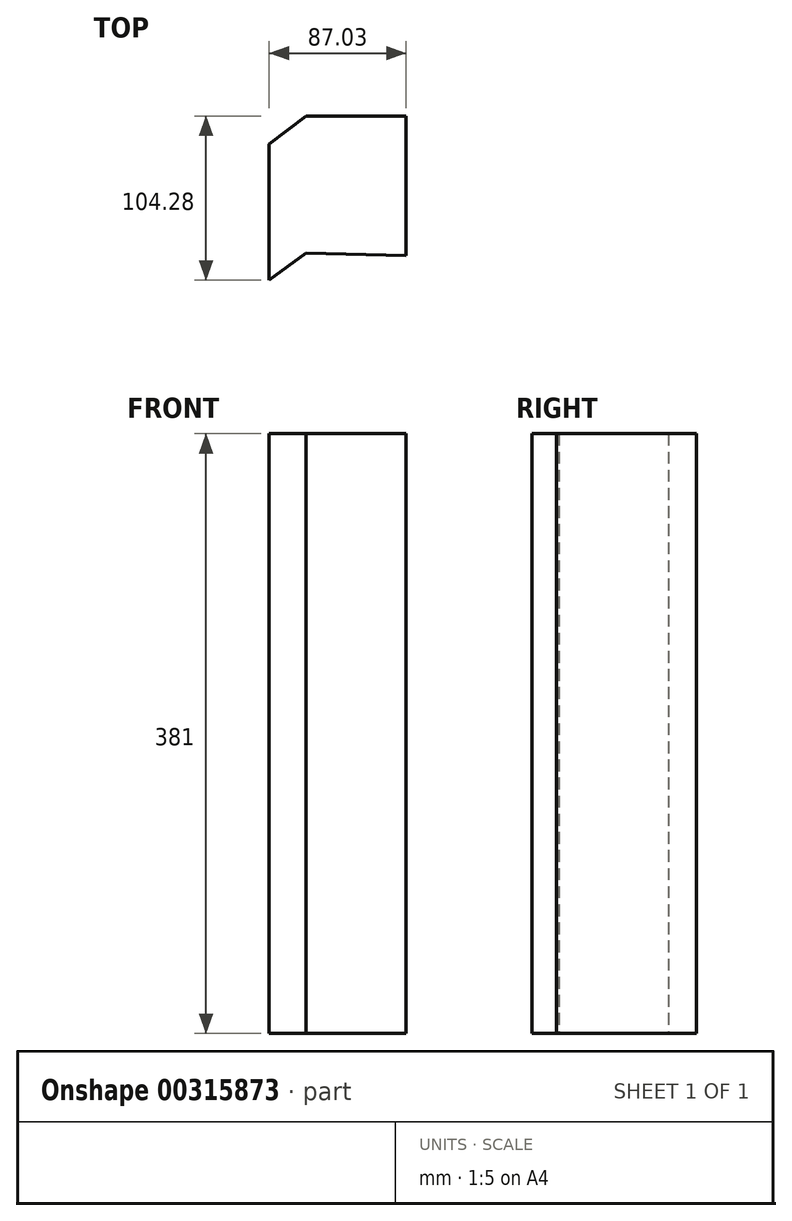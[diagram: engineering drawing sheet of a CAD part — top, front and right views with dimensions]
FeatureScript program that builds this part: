
annotation { "Feature Type Name" : "Feature", "Feature Type Description" : "" }
export const myFeature = defineFeature(function(context is Context, id is Id, definition is map)
    precondition{}
    {
        {
            var Q0;
            Q0=qCreatedBy(makeId("Top.planeOp"),FACE);
            var sketch = newSketch(context, id + "F0", { "sketchPlane" : qUnion([Q0])});
            skLineSegment(sketch, "E0", {"start": v(-30.9, 48.92) * mm, "end": v(-30.9, -38.3) * mm});
            skLineSegment(sketch, "E1", {"start": v(-30.9, 48.92) * mm, "end": v(32.61, 48.92) * mm});
            skLineSegment(sketch, "E2", {"start": v(32.61, 48.92) * mm, "end": v(32.61, -39.82) * mm});
            skLineSegment(sketch, "E3", {"start": v(32.61, -39.82) * mm, "end": v(-30.9, -38.3) * mm});
            skLineSegment(sketch, "E4", {"start": v(-30.9, 48.92) * mm, "end": v(-54.42, 31.1) * mm});
            skLineSegment(sketch, "E5", {"start": v(-54.42, 31.1) * mm, "end": v(-54.42, -55.36) * mm});
            skLineSegment(sketch, "E6", {"start": v(-54.42, -55.36) * mm, "end": v(-30.9, -38.3) * mm});
            skSolve(sketch);
        }
        {
            var Q0;
            Q0=makeQuery(id+"F0.imprint","IMPRINT",FACE,{"disambiguationData":[TD([[makeQuery(id+"F0.imprint","IMPRINT",EDGE,{"derivedFrom":sQuery(id+"F0.wireOp",EDGE,"E0")}),-1.0]])]});
            var Q1;
            Q1=makeQuery(id+"F0.imprint","IMPRINT",FACE,{"disambiguationData":[TD([[makeQuery(id+"F0.imprint","IMPRINT",EDGE,{"derivedFrom":sQuery(id+"F0.wireOp",EDGE,"E0")}),1.0]])]});
            extrude(context, id + "F1", {"entities" : qUnion([Q0, Q1]), "depth" : 381 * mm});
        }
    });
